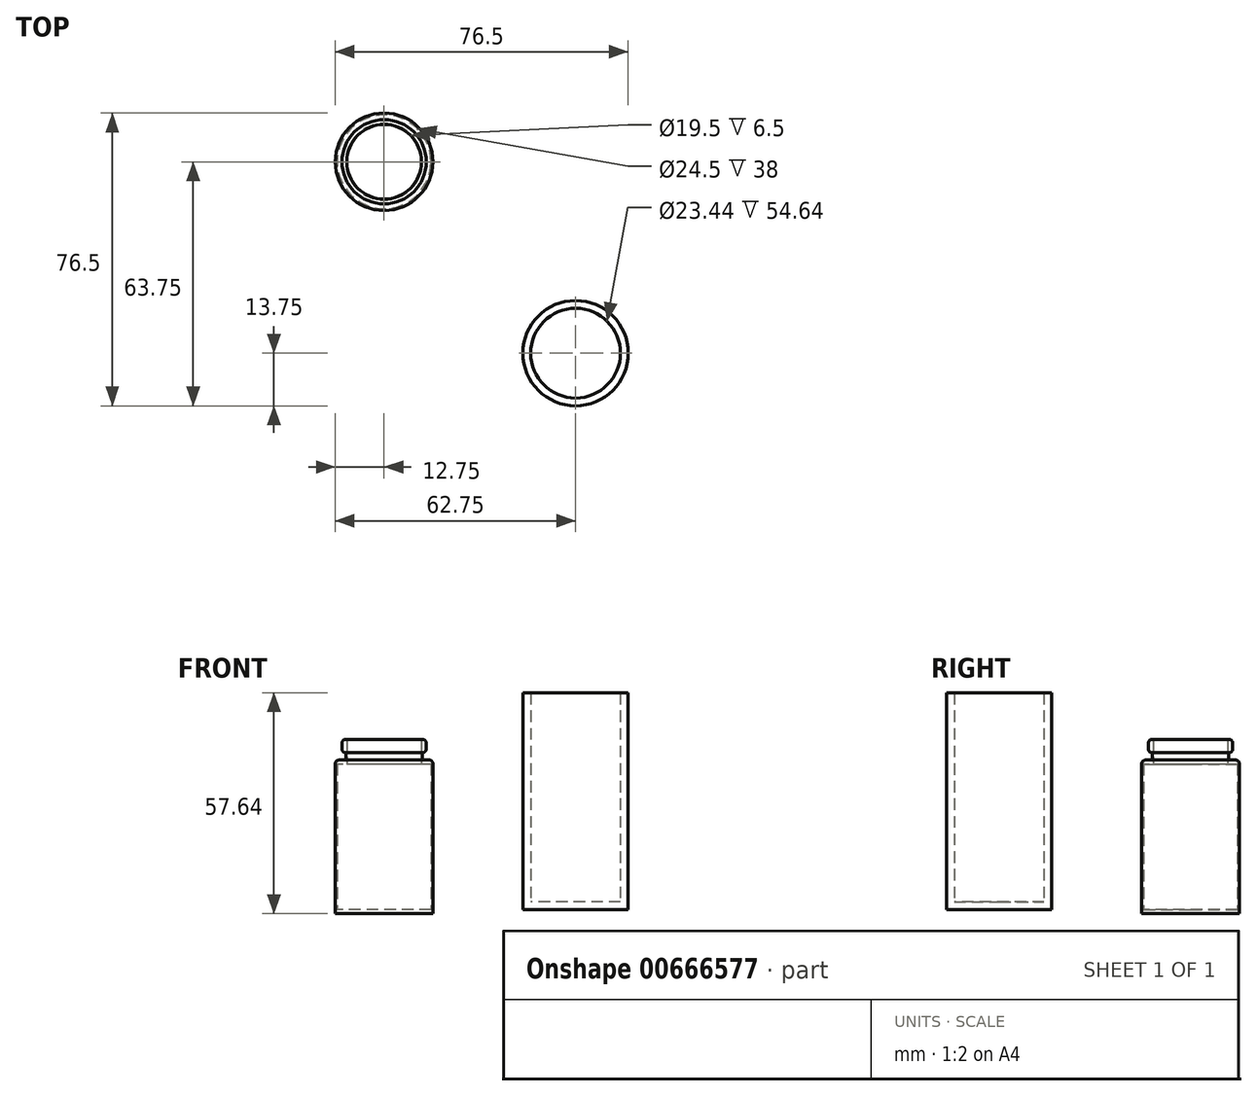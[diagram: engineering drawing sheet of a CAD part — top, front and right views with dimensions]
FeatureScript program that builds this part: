
annotation { "Feature Type Name" : "Feature", "Feature Type Description" : "" }
export const myFeature = defineFeature(function(context is Context, id is Id, definition is map)
    precondition{}
    {
        {
            var Q0;
            Q0=qCreatedBy(makeId("Top.planeOp"),FACE);
            var sketch = newSketch(context, id + "F0", { "sketchPlane" : qUnion([Q0])});
            skCircle(sketch, "E0", {"center": v(0, 0) * mm, "radius": 13.75 * mm});
            skCircle(sketch, "E1", {"center": v(0, 0) * mm, "radius": 11.72 * mm});
            skSolve(sketch);
        }
        {
            var Q0;
            Q0=makeQuery(id+"F0.imprint","IMPRINT",FACE,{"disambiguationData":[TD([[makeQuery(id+"F0.imprint","IMPRINT",EDGE,{"derivedFrom":sQuery(id+"F0.wireOp",EDGE,"E0")}),1.0]])]});
            var Q1;
            Q1=makeQuery(id+"F0.imprint","IMPRINT",FACE,{"disambiguationData":[TD([[makeQuery(id+"F0.imprint","IMPRINT",EDGE,{"derivedFrom":sQuery(id+"F0.wireOp",EDGE,"E1")}),1.0]])]});
            extrude(context, id + "F1", {"entities" : qUnion([Q0, Q1]), "depth" : 2 * mm, "offsetDistance" : 25 * mm});
        }
        {
            var Q0;
            Q0=makeQuery(id+"F0.imprint","IMPRINT",FACE,{"disambiguationData":[TD([[makeQuery(id+"F0.imprint","IMPRINT",EDGE,{"derivedFrom":sQuery(id+"F0.wireOp",EDGE,"E0")}),1.0]])]});
            extrude(context, id + "F2", {"entities" : qUnion([Q0]), "operationType" : NewBodyOperationType.ADD, "depth" : 56.64 * mm, "offsetDistance" : 25 * mm});
        }
        {
            var Q0;
            Q0=qCreatedBy(makeId("Top.planeOp"),FACE);
            var sketch = newSketch(context, id + "F3", { "sketchPlane" : qUnion([Q0])});
            skLineSegment(sketch, "E2", {"start": v(-127.25, 50) * mm, "end": v(94.88, 50) * mm, "construction": true});
            skLineSegment(sketch, "E3", {"start": v(-50, 62.51) * mm, "end": v(-50, -43.4) * mm, "construction": true});
            skCircle(sketch, "E4", {"center": v(-50, 50) * mm, "radius": 12.75 * mm});
            skCircle(sketch, "E5", {"center": v(-50, 50) * mm, "radius": 12.25 * mm});
            skSolve(sketch);
        }
        {
            var Q0;
            Q0=makeQuery(id+"F3.imprint","IMPRINT",FACE,{"disambiguationData":[TD([[makeQuery(id+"F3.imprint","IMPRINT",EDGE,{"derivedFrom":sQuery(id+"F3.wireOp",EDGE,"E4")}),1.0]])]});
            extrude(context, id + "F4", {"entities" : qUnion([Q0]), "depth" : 38 * mm, "offsetDistance" : 25 * mm, "hasSecondDirection" : true, "secondDirectionOppositeDirection" : true, "secondDirectionDepth" : 1 * mm});
        }
        {
            var Q0;
            Q0=makeQuery(id+"F3.imprint","IMPRINT",FACE,{"disambiguationData":[TD([[makeQuery(id+"F3.imprint","IMPRINT",EDGE,{"derivedFrom":sQuery(id+"F3.wireOp",EDGE,"E5")}),1.0]])]});
            extrude(context, id + "F5", {"entities" : qUnion([Q0]), "operationType" : NewBodyOperationType.ADD, "oppositeDirection" : true, "depth" : 1 * mm, "offsetDistance" : 25 * mm});
        }
        {
            var Q0;
            Q0=makeQuery(id+"F4.opExtrude","CAP_FACE",FACE,{"disambiguationData":[OSD([sQuery(id+"F3.wireOp",EDGE,"E4"),sQuery(id+"F3.wireOp",EDGE,"E5")])],"isStart":false});
            var sketch = newSketch(context, id + "F6", { "sketchPlane" : qUnion([Q0])});
            skCircle(sketch, "E6", {"center": v(-50, 50) * mm, "radius": 10 * mm});
            skCircle(sketch, "E7", {"center": v(-50, 50) * mm, "radius": 12.75 * mm});
            skCircle(sketch, "E8", {"center": v(-50, 50) * mm, "radius": 9.75 * mm});
            skSolve(sketch);
        }
        {
            var Q0;
            Q0 = qSketchRegion(id + "F6", true);
            var Q1;
            Q1=makeQuery(id+"F6.imprint","IMPRINT",FACE,{"disambiguationData":[TD([[makeQuery(id+"F6.imprint","IMPRINT",EDGE,{"derivedFrom":sQuery(id+"F6.wireOp",EDGE,"E6")}),1.0]])]});
            extrude(context, id + "F7", {"entities" : qUnion([Q0, Q1]), "operationType" : NewBodyOperationType.ADD, "depth" : 1.1 * mm, "offsetDistance" : 25 * mm});
        }
        {
            var Q0;
            Q0=makeQuery(id+"F6.imprint","IMPRINT",FACE,{"disambiguationData":[TD([[makeQuery(id+"F6.imprint","IMPRINT",EDGE,{"derivedFrom":sQuery(id+"F6.wireOp",EDGE,"E6")}),1.0]])]});
            extrude(context, id + "F8", {"entities" : qUnion([Q0]), "operationType" : NewBodyOperationType.ADD, "depth" : 3 * mm, "offsetDistance" : 25 * mm});
        }
        {
            var Q0;
            Q0=makeQuery(id+"F8.opExtrude","CAP_FACE",FACE,{"disambiguationData":[OSD([sQuery(id+"F6.wireOp",EDGE,"E6"),sQuery(id+"F6.wireOp",EDGE,"E8")])],"isStart":false});
            var sketch = newSketch(context, id + "F9", { "sketchPlane" : qUnion([Q0])});
            skCircle(sketch, "E9", {"center": v(-50, 50) * mm, "radius": 11 * mm});
            skCircle(sketch, "E10", {"center": v(-50, 50) * mm, "radius": 10 * mm});
            skCircle(sketch, "E11", {"center": v(-50, 50) * mm, "radius": 9.75 * mm});
            skSolve(sketch);
        }
        {
            var Q0;
            Q0 = qSketchRegion(id + "F9", true);
            var Q1;
            Q1=makeQuery(id+"F9.imprint","IMPRINT",FACE,{"disambiguationData":[TD([[makeQuery(id+"F9.imprint","IMPRINT",EDGE,{"derivedFrom":sQuery(id+"F9.wireOp",EDGE,"E10")}),1.0]])]});
            extrude(context, id + "F10", {"entities" : qUnion([Q0, Q1]), "operationType" : NewBodyOperationType.ADD, "depth" : 3.5 * mm, "offsetDistance" : 25 * mm});
        }
        {
            var Q0;
            Q0=makeQuery(id+"F7.opExtrude","CAP_EDGE",EDGE,{"disambiguationData":[OSD([sQuery(id+"F6.wireOp",EDGE,"E7")])],"isStart":false});
            fillet(context, id + "F11", {"entities" : qUnion([Q0]), "radius" : 1 * mm, "tangentPropagation" : true, "allowEdgeOverflow" : false});
        }
        {
            var Q0;
            Q0=makeQuery(id+"F10.opExtrude","CAP_EDGE",EDGE,{"disambiguationData":[OSD([sQuery(id+"F9.wireOp",EDGE,"E9")])],"isStart":true});
            var Q1;
            Q1=makeQuery(id+"F10.opExtrude","CAP_EDGE",EDGE,{"disambiguationData":[OSD([sQuery(id+"F9.wireOp",EDGE,"E9")])],"isStart":false});
            fillet(context, id + "F12", {"entities" : qUnion([Q0, Q1]), "radius" : 1 * mm, "tangentPropagation" : true, "allowEdgeOverflow" : false});
        }
    });
